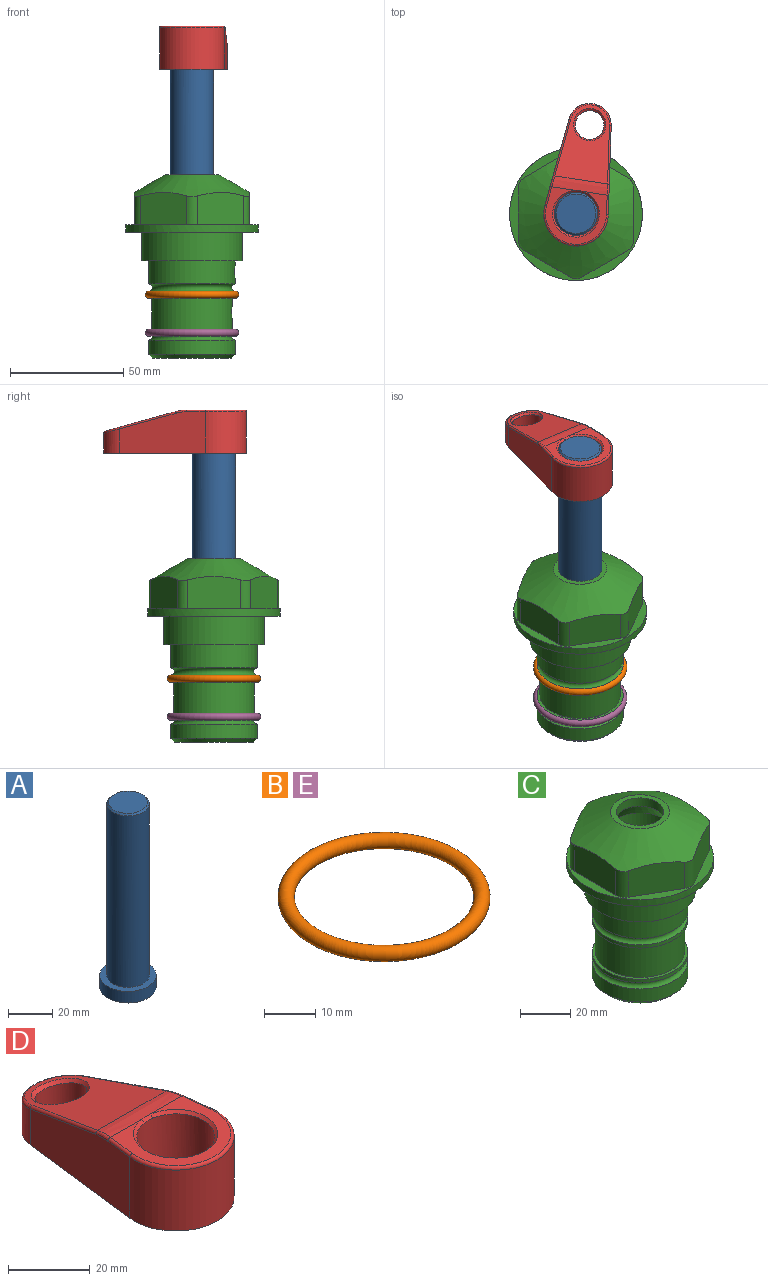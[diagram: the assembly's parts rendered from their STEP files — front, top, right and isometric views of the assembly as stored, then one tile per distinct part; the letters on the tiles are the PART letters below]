
ASSEMBLY  parts=5 mates=4
PART A: 6 faces, bbox 25.4x25.4x101.6 mm
  f0: plane 17.46x17.46mm, normal (0,0,1), area 239.5mm2, adj f5
  f1: plane 25.4x25.4mm, normal (0,0,-1), area 506.7mm2, adj f2
  f2: cylinder r=12.7mm len=25.4mm, axis (0,0,1), area 506.7mm2, adj f1,f3
  f3: plane 25.4x25.4mm, normal (0,0,1), area 221.7mm2, adj f2,f4
  f4: cylinder r=9.53mm len=94.46mm, axis (0,0,1), area 5653mm2, adj f3,f5
  f5: cone r=8.73mm half-angle=45deg, axis (0,0,-1), area 64.4mm2, adj f0,f4
PART B: 1 faces, bbox 44.7x44.7x3.2 mm
  f0: torus R=19.05mm, axis (0,0,1), area 1193.9mm2
PART C: 36 faces, bbox 58.7x58.7x81 mm
  f0: cylinder r=17.78mm len=35.56mm, axis (0,0,1), area 1670.8mm2, adj f23,f24,f31
  f1: cylinder r=19.05mm len=38.1mm, axis (0,0,1), area 1191.9mm2, adj f26,f27,f30
  f2: plane 58.66x58.66mm, normal (0,0,-1), area 1150.6mm2, adj f3,f28
  f3: cylinder r=29.33mm len=58.66mm, axis (0,0,-1), area 585.1mm2, adj f2,f4
  f4: plane 58.66x58.66mm, normal (0,0,1), area 475.9mm2, adj f3,f5,f6,f7,f8,f9,f10,f11
  f5: plane 20.32x14.34mm, normal (-0.5,0.87,0), area 324.4mm2, adj f4,f15,f16,f17
  f6: plane 20.32x14.34mm, normal (0.5,0.87,0), area 324.4mm2, adj f4,f14,f15,f17
  f7: plane 23.48x14.34mm, normal (1,0,0), area 324.4mm2, adj f4,f13,f14,f17
  f8: plane 20.32x14.34mm, normal (0.5,-0.87,0), area 324.4mm2, adj f4,f12,f13,f17
  f9: plane 20.32x14.34mm, normal (-0.5,-0.87,0), area 324.4mm2, adj f4,f11,f12,f17
  f10: plane 23.48x14.34mm, normal (-1,0,0), area 324.4mm2, adj f4,f11,f16,f17
  f11: cylinder r=5.08mm len=12.85mm, axis (0,0,-1), area 67.2mm2, adj f4,f9,f10,f17
  f12: cylinder r=5.08mm len=12.85mm, axis (0,0,-1), area 67.2mm2, adj f4,f8,f9,f17
  f13: cylinder r=5.08mm len=12.85mm, axis (0,0,-1), area 67.2mm2, adj f4,f7,f8,f17
  f14: cylinder r=5.08mm len=12.85mm, axis (0,0,-1), area 67.2mm2, adj f4,f6,f7,f17
  f15: cylinder r=5.08mm len=12.85mm, axis (0,0,-1), area 67.2mm2, adj f4,f5,f6,f17
  f16: cylinder r=5.08mm len=12.85mm, axis (0,0,-1), area 67.2mm2, adj f4,f5,f10,f17
  f17: cone r=11.73mm half-angle=60deg, axis (0,0,-1), area 2071.8mm2, adj f5,f6,f7,f8,f9,f10,f11,f12
  f18: plane 23.46x23.46mm, normal (0,0,1), area 147.4mm2, adj f17,f35
  f19: plane 34.93x34.93mm, normal (0,0,-1), area 958mm2, adj f29
  f20: cylinder r=19.05mm len=38.1mm, axis (0,0,1), area 760.1mm2, adj f21,f29
  f21: torus R=19.05mm, axis (0,0,1), area 565.3mm2, adj f20,f22
  f22: cylinder r=19.05mm len=38.1mm, axis (0,0,1), area 190mm2, adj f21,f23
  f23: plane 38.1x38.1mm, normal (0,0,1), area 146.9mm2, adj f0,f22
  f24: plane 38.1x38.1mm, normal (0,0,-1), area 146.9mm2, adj f0,f25
  f25: cylinder r=19.05mm len=38.1mm, axis (0,0,1), area 190mm2, adj f24,f26
  f26: torus R=19.05mm, axis (0,0,1), area 565.3mm2, adj f1,f25
  f27: plane 44.45x44.45mm, normal (0,0,-1), area 411.7mm2, adj f1,f28
  f28: cylinder r=22.23mm len=44.45mm, axis (0,0,1), area 1773.5mm2, adj f2,f27
  f29: cone r=19.05mm half-angle=45deg, axis (0,0,1), area 257.5mm2, adj f19,f20
  f30: cylinder r=3.17mm len=6.75mm, axis (-1,0,0), area 128mm2, adj f1,f33
  f31: cylinder r=3.17mm len=6.35mm, axis (-1,0,0), area 102.5mm2, adj f0,f33
  f32: plane 25.4x25.4mm, normal (0,0,1), area 506.7mm2, adj f33
  f33: cylinder r=12.7mm len=66.42mm, axis (0,0,-1), area 5236.2mm2, adj f30,f31,f32,f34
  f34: cone r=9.53mm half-angle=30deg, axis (0,0,-1), area 443.4mm2, adj f33,f35
  f35: cylinder r=9.53mm len=19.05mm, axis (0,0,-1), area 240.9mm2, adj f18,f34
PART D: 31 faces, bbox 31.7x65.5x19.8 mm
  f0: plane 39.12x18.26mm, normal (0.99,0.12,0), area 612.2mm2, adj f1,f4,f7,f11,f13,f15
  f1: cylinder r=9.53mm len=18.91mm, axis (0,0,-1), area 296.1mm2, adj f0,f2,f7,f17
  f2: plane 39.12x18.26mm, normal (-0.99,0.12,0), area 612.2mm2, adj f1,f4,f7,f12,f14,f16
  f3: cylinder r=6.35mm len=12.7mm, axis (0,0,-1), area 362.4mm2, adj f7,f18
  f4: cylinder r=14.29mm len=28.58mm, axis (0,0,-1), area 882.2mm2, adj f0,f2,f7,f10
  f5: cylinder r=9.53mm len=19.05mm, axis (0,0,-1), area 1092.6mm2, adj f7,f19,f20
  f6: plane 26.99x23.69mm, normal (0,0,1), area 216.2mm2, adj f9,f10,f11,f12,f19
  f7: plane 63.5x28.58mm, normal (0,0,-1), area 661.8mm2, adj f0,f1,f2,f3,f4,f5,f22,f23
  f8: plane 33.52x23.6mm, normal (0,0.26,0.97), area 486mm2, adj f9,f15,f16,f17,f18
  f9: cylinder r=19.05mm len=24.72mm, axis (1,0,0), area 120.4mm2, adj f6,f8,f13,f14,f20
  f10: torus R=13.49mm, axis (0,0,1), area 59mm2, adj f4,f6,f11,f12
  f11: cylinder r=0.79mm len=8.67mm, axis (0.12,-0.99,0), area 10.8mm2, adj f0,f6,f10,f13
  f12: cylinder r=0.79mm len=8.67mm, axis (0.12,0.99,0), area 10.8mm2, adj f2,f6,f10,f14
  f13: bspline ~4.95x1.42mm, area 6.1mm2, adj f0,f9,f11,f15
  f14: bspline ~4.95x1.42mm, area 6.1mm2, adj f2,f9,f12,f16
  f15: cylinder r=0.79mm len=25.95mm, axis (0.12,-0.96,0.26), area 32.9mm2, adj f0,f8,f13,f17
  f16: cylinder r=0.79mm len=25.95mm, axis (0.12,0.96,-0.26), area 32.9mm2, adj f2,f8,f14,f17
  f17: bspline ~18.91x8.38mm, area 30mm2, adj f1,f8,f15,f16
  f18: bspline ~14.29x14.29mm, area 48.3mm2, adj f3,f8
  f19: cone r=9.53mm half-angle=45deg, axis (0,0,1), area 66.5mm2, adj f5,f6,f20
  f20: bspline ~3.22x0.96mm, area 3.5mm2, adj f5,f9,f19
  f21: plane 2.75x2.72mm, normal (0,0,-1), area 2.9mm2, adj f23,f25,f28
  f22: plane 23.05x15.88mm, normal (-0.99,-0.12,0), area 323.6mm2, adj f7,f25,f26,f27,f28,f29
  f23: plane 23.05x15.88mm, normal (0.99,-0.12,0), area 323.6mm2, adj f7,f21,f25,f27,f28,f30
  f24: cylinder r=9.53mm len=10.69mm, axis (0,0,-1), area 114.7mm2, adj f7,f27,f29,f30
  f25: cylinder r=12.7mm len=20.59mm, axis (0,0,-1), area 381.1mm2, adj f7,f21,f22,f23,f26,f28
  f26: plane 2.75x2.72mm, normal (0,0,-1), area 2.9mm2, adj f22,f25,f28
  f27: plane 19.72x18.37mm, normal (0,-0.26,-0.97), area 291.8mm2, adj f22,f23,f24,f28,f29,f30
  f28: cylinder r=15.88mm len=19.92mm, axis (1,0,0), area 54.8mm2, adj f21,f22,f23,f25,f26,f27
  f29: cylinder r=1.59mm len=11mm, axis (0,0,-1), area 34.7mm2, adj f7,f22,f24,f27
  f30: cylinder r=1.59mm len=11mm, axis (0,0,-1), area 34.7mm2, adj f7,f23,f24,f27
PART E: same geometry as B
PLACE A rot(axis=(0,0,-1),8.8deg) t=(0,0,27.55)mm
PLACE B t=(0,0,-3.18)mm
PLACE C at identity fixed
PLACE D rot(axis=(0,0,-1),8.8deg) t=(0,0,27.55)mm
PLACE E t=(0,0,-20)mm
MATE cylindrical C.f0 <-> A.f2  axis (0,0,1) through (0,0,-50.55)mm
MATE fastened E.f0 <-> C.f0  axis (0,0,1) through (0,0,-44.51)mm
MATE fastened B.f0 <-> C.f0  axis (0,0,1) through (0,0,-27.69)mm
MATE fastened D.f4 <-> A.f2  axis (0,0,1) through (0,0,91.05)mm
